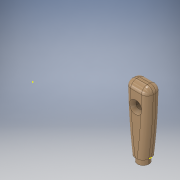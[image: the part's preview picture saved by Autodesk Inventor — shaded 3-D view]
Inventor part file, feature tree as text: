
AUTODESK INVENTOR PART (.ipt)
format: ipt  version: 2018 (Build 220112000, 112)  size: 209,920 bytes
history: native  units: in
note: dims shown in document units (in); Inventor stores cm internally (conversion verified against a paired STEP export)
features: sketch x6, extrude x2, hole x2, fillet x1, plane x1, revolve x1
ambient origin geometry x8: Origin, YZ Plane, XZ Plane, XY Plane, X Axis, Y Axis, Z Axis, Center Point
bodies: Solid1 (feature_tree)
feature tree (13):
  sketch  "Sketch1"  dims[d0=1.1525in d2=0.7in d3=0.739in d4=0.0in]
  extrude  "Extrusion1"  Depth=0.7in
  fillet  "Fillet1"  Radius=0.739in
  sketch  "Sketch2"  dims[d5=0.3in d11=90.0deg]
  plane  "Work Plane1"
  revolve  "Revolution2"  Angle=90.0deg
  extrude  "Extrusion2"  TaperAngle=90.0deg  [1 undecoded]
  hole  "Hole1"  [1 undecoded]
  hole  "Hole2"  [1 undecoded]
  sketch  "Sketch3"  dims[d14=3.0055in d15=90.0deg]
  sketch  "Sketch4"  dims[d17=0.145in d18=0.05in]
  sketch  "Sketch5"  dims[d19=0.639in d20=0.0in d23=0.6565in]
  sketch  "Sketch6"  dims[d24=0.33in d25=0.75in d26=0.645in d27=0.25in d28=0.5635in d29=1.0in d30=0.8108in d31=0.33in d32=0.75in d33=0.7075in d34=0.25in d35=0.5635in d36=1.0in d37=0.8108in]
note: 3 required parameter values undecoded (feature->parameter linkage not recoverable at this tier; creation-order binding heuristic only, values carry confidence <= 0.55)
